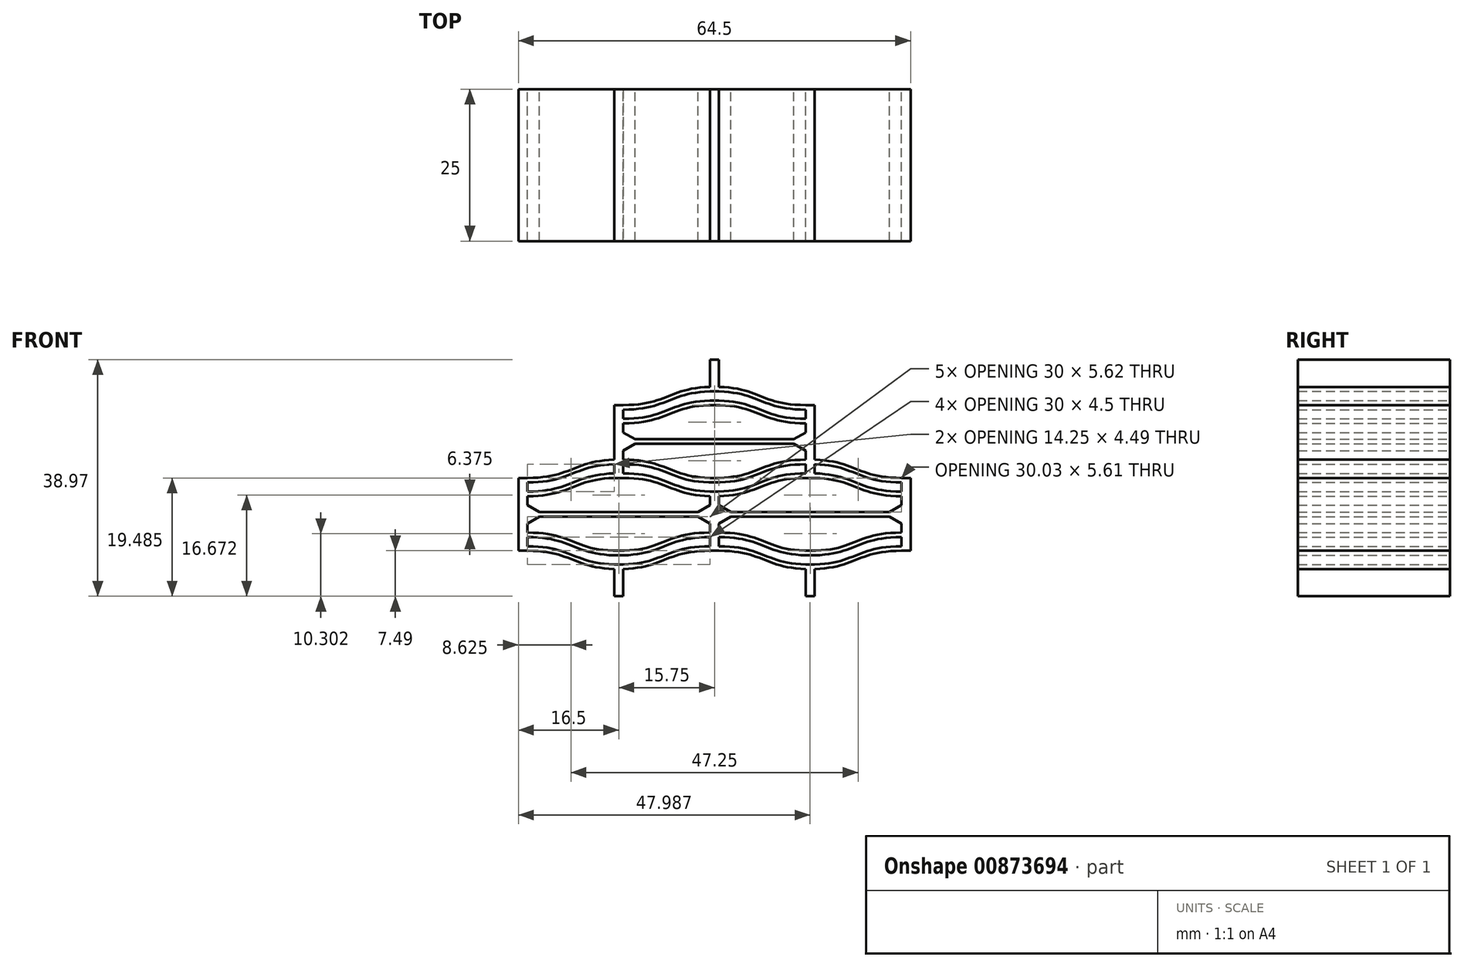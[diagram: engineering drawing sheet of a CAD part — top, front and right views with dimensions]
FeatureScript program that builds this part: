
annotation { "Feature Type Name" : "Feature", "Feature Type Description" : "" }
export const myFeature = defineFeature(function(context is Context, id is Id, definition is map)
    precondition{}
    {
        {
            var Q0;
            Q0=qCreatedBy(makeId("Front.planeOp"),FACE);
            var sketch = newSketch(context, id + "F0", { "sketchPlane" : qUnion([Q0])});
            skLineSegment(sketch, "E0", {"start": v(0, 0) * mm, "end": v(0, -12) * mm});
            skLineSegment(sketch, "E1", {"start": v(0, -12) * mm, "end": v(1.5, -12) * mm});
            skLineSegment(sketch, "E2", {"start": v(0, 0) * mm, "end": v(1.5, 0) * mm});
            skLineSegment(sketch, "E3", {"start": v(33, 0) * mm, "end": v(31.5, 0) * mm});
            skLineSegment(sketch, "E4", {"start": v(33, -12) * mm, "end": v(31.5, -12) * mm});
            skPoint(sketch, "E5", {"position": v(0, -6) * mm});
            skLineSegment(sketch, "E6", {"start": v(1.5, -0.75) * mm, "end": v(1.5, -2.25) * mm});
            skPoint(sketch, "E7", {"position": v(0, -4.5) * mm});
            skPoint(sketch, "E8", {"position": v(0, -7.5) * mm});
            skLineSegment(sketch, "E9", {"start": v(1.5, -7.5) * mm, "end": v(3.45, -6.38) * mm});
            skLineSegment(sketch, "E10", {"start": v(1.5, -4.5) * mm, "end": v(3.45, -5.62) * mm});
            skPoint(sketch, "E11", {"position": v(31.5, -7.5) * mm});
            skPoint(sketch, "E12", {"position": v(31.5, -4.5) * mm});
            skLineSegment(sketch, "E13", {"start": v(31.5, -4.5) * mm, "end": v(29.55, -5.62) * mm});
            skLineSegment(sketch, "E14", {"start": v(29.55, -6.37) * mm, "end": v(31.5, -7.5) * mm});
            skPoint(sketch, "E15.positionSnap0", {"position": v(16.5, -5.62) * mm});
            skPoint(sketch, "E16", {"position": v(0, -3) * mm});
            skPoint(sketch, "E17", {"position": v(0, -9) * mm});
            skPoint(sketch, "E18", {"position": v(0, -2.25) * mm});
            skPoint(sketch, "E19", {"position": v(0, -9.75) * mm});
            skPoint(sketch, "E20", {"position": v(1.5, -0.75) * mm});
            skPoint(sketch, "E21", {"position": v(1.5, -11.25) * mm});
            skPoint(sketch, "E22", {"position": v(1.5, -2.25) * mm});
            skPoint(sketch, "E23", {"position": v(1.5, -3) * mm});
            skPoint(sketch, "E24", {"position": v(1.5, -9.75) * mm});
            skPoint(sketch, "E25", {"position": v(1.5, -9) * mm});
            skPoint(sketch, "E26", {"position": v(31.5, -9) * mm});
            skPoint(sketch, "E27", {"position": v(31.5, -9.75) * mm});
            skPoint(sketch, "E28", {"position": v(31.5, -11.25) * mm});
            skLineSegment(sketch, "E29.trimOffspring", {"start": v(3.45, -5.63) * mm, "end": v(16.5, -5.62) * mm});
            skLineSegment(sketch, "E30.trimOffspring", {"start": v(3.45, -6.38) * mm, "end": v(29.55, -6.37) * mm});
            skPoint(sketch, "E31.start.orphan", {"position": v(0, -6.38) * mm});
            skPoint(sketch, "E32.start.orphan", {"position": v(0, -5.62) * mm});
            skLineSegment(sketch, "E33.trimOffspring", {"start": v(1.5, -3) * mm, "end": v(1.5, -4.5) * mm});
            skLineSegment(sketch, "E34.trimOffspring", {"start": v(1.5, -9.75) * mm, "end": v(1.5, -11.25) * mm});
            skPoint(sketch, "E35.trimOffspring.end.orphan", {"position": v(33, -6.37) * mm});
            skPoint(sketch, "E36.trimOffspring.end.orphan", {"position": v(33, -5.62) * mm});
            skLineSegment(sketch, "E37.trimOffspring", {"start": v(31.5, -9.75) * mm, "end": v(31.5, -11.25) * mm});
            skLineSegment(sketch, "E38.trimOffspring", {"start": v(1.5, -7.5) * mm, "end": v(1.5, -9) * mm});
            skLineSegment(sketch, "E39.trimOffspring", {"start": v(31.5, -7.5) * mm, "end": v(31.5, -9) * mm});
            skLineSegment(sketch, "E40", {"start": v(16.5, -5.62) * mm, "end": v(29.55, -5.62) * mm});
            skPoint(sketch, "E41", {"position": v(16.5, -3) * mm});
            skPoint(sketch, "E42", {"position": v(16.5, 0) * mm});
            skPoint(sketch, "E43", {"position": v(9, -3) * mm});
            skPoint(sketch, "E44", {"position": v(9, -1.5) * mm});
            skPoint(sketch, "E45", {"position": v(24, -1.5) * mm});
            skFitSpline(sketch, "E46", {"points": [v(1.5, -3) * mm, v(9, -1.5) * mm, v(16.5, 0) * mm], "startDerivative": vector(22.5, 0) * mm, "endDerivative": vector(22.5, 0) * mm});
            skFitSpline(sketch, "E47", {"points": [v(16.5, 0) * mm, v(24, -1.5) * mm, v(31.5, -3) * mm], "startDerivative": vector(22.5, 0) * mm, "endDerivative": vector(22.5, 0) * mm});
            skFitSpline(sketch, "E48", {"points": [v(1.5, -2.25) * mm, v(9, -0.75) * mm, v(16.5, 0.75) * mm], "startDerivative": vector(22.5, 0) * mm, "endDerivative": vector(22.5, 0) * mm});
            skFitSpline(sketch, "E49", {"points": [v(1.5, -0.75) * mm, v(9, 0.75) * mm, v(16.5, 2.25) * mm], "startDerivative": vector(22.5, 0) * mm, "endDerivative": vector(22.5, 0) * mm});
            skFitSpline(sketch, "E50", {"points": [v(1.5, 0) * mm, v(9, 1.5) * mm, v(16.5, 3) * mm], "startDerivative": vector(22.5, 0) * mm, "endDerivative": vector(22.5, 0) * mm});
            skFitSpline(sketch, "E51", {"points": [v(31.5, -9) * mm, v(24, -10.5) * mm, v(16.5, -12) * mm], "startDerivative": vector(-22.5, 0) * mm, "endDerivative": vector(-22.5, 0) * mm});
            skFitSpline(sketch, "E52", {"points": [v(16.5, -12) * mm, v(9, -10.5) * mm, v(1.5, -9) * mm], "startDerivative": vector(-22.5, 0) * mm, "endDerivative": vector(-22.5, 0) * mm});
            skFitSpline(sketch, "E53", {"points": [v(31.5, -9.75) * mm, v(24, -11.25) * mm, v(16.5, -12.75) * mm], "startDerivative": vector(-22.5, 0) * mm, "endDerivative": vector(-22.5, 0) * mm});
            skFitSpline(sketch, "E54", {"points": [v(16.5, -12.75) * mm, v(9, -11.25) * mm, v(1.5, -9.75) * mm], "startDerivative": vector(-22.5, 0) * mm, "endDerivative": vector(-22.5, 0) * mm});
            skFitSpline(sketch, "E55", {"points": [v(31.5, -11.25) * mm, v(24, -12.75) * mm, v(16.5, -14.25) * mm], "startDerivative": vector(-22.5, 0) * mm, "endDerivative": vector(-22.5, 0) * mm});
            skFitSpline(sketch, "E56", {"points": [v(16.5, -14.25) * mm, v(9, -12.75) * mm, v(1.5, -11.25) * mm], "startDerivative": vector(-22.5, 0) * mm, "endDerivative": vector(-22.5, 0) * mm});
            skFitSpline(sketch, "E57", {"points": [v(31.5, -12) * mm, v(24, -13.5) * mm, v(16.5, -15) * mm], "startDerivative": vector(-22.5, 0) * mm, "endDerivative": vector(-22.5, 0) * mm});
            skFitSpline(sketch, "E58", {"points": [v(16.5, -15) * mm, v(9, -13.5) * mm, v(1.5, -12) * mm], "startDerivative": vector(-22.5, 0) * mm, "endDerivative": vector(-22.5, 0) * mm});
            skPoint(sketch, "E59", {"position": v(15.75, -12.34) * mm});
            skPoint(sketch, "E60", {"position": v(17.25, -12.34) * mm});
            skLineSegment(sketch, "E61", {"start": v(15.75, -12.74) * mm, "end": v(15.75, -14.24) * mm});
            skLineSegment(sketch, "E62", {"start": v(17.25, -12.74) * mm, "end": v(17.25, -14.24) * mm});
            skLineSegment(sketch, "E63", {"start": v(15.75, -14.99) * mm, "end": v(15.75, -19.49) * mm});
            skLineSegment(sketch, "E64", {"start": v(15.75, 0.74) * mm, "end": v(15.75, 2.24) * mm});
            skLineSegment(sketch, "E65", {"start": v(17.25, 2.24) * mm, "end": v(17.25, 0.74) * mm});
            skLineSegment(sketch, "E66", {"start": v(15.75, -19.49) * mm, "end": v(17.25, -19.49) * mm});
            skLineSegment(sketch, "E67", {"start": v(17.25, -19.49) * mm, "end": v(17.25, -14.99) * mm});
            skPoint(sketch, "E68", {"position": v(15.75, 2.99) * mm});
            skPoint(sketch, "E69", {"position": v(17.25, 2.99) * mm});
            skLineSegment(sketch, "E70", {"start": v(15.75, 2.99) * mm, "end": v(15.75, 7.49) * mm});
            skLineSegment(sketch, "E71", {"start": v(17.25, 4.49) * mm, "end": v(17.25, 2.99) * mm});
            skLineSegment(sketch, "E72", {"start": v(64.5, 0) * mm, "end": v(64.5, -12) * mm});
            skLineSegment(sketch, "E73", {"start": v(31.5, -12) * mm, "end": v(33, -12) * mm});
            skLineSegment(sketch, "E74", {"start": v(31.5, 0) * mm, "end": v(33, 0) * mm});
            skLineSegment(sketch, "E75", {"start": v(64.5, 0) * mm, "end": v(63, 0) * mm});
            skLineSegment(sketch, "E76", {"start": v(64.5, -12) * mm, "end": v(63, -12) * mm});
            skPoint(sketch, "E77", {"position": v(31.5, -6) * mm});
            skLineSegment(sketch, "E78", {"start": v(63, -0.75) * mm, "end": v(63, -2.25) * mm});
            skLineSegment(sketch, "E79", {"start": v(33, -7.5) * mm, "end": v(34.95, -6.37) * mm});
            skLineSegment(sketch, "E80", {"start": v(32.97, -4.5) * mm, "end": v(34.95, -5.62) * mm});
            skPoint(sketch, "E81", {"position": v(63, -7.5) * mm});
            skPoint(sketch, "E82", {"position": v(63, -4.5) * mm});
            skLineSegment(sketch, "E83", {"start": v(63, -4.5) * mm, "end": v(61.05, -5.62) * mm});
            skLineSegment(sketch, "E84", {"start": v(61.05, -6.37) * mm, "end": v(63, -7.5) * mm});
            skPoint(sketch, "E85.positionSnap0", {"position": v(48, -5.62) * mm});
            skPoint(sketch, "E86", {"position": v(33, -11.25) * mm});
            skPoint(sketch, "E87", {"position": v(33, -9.75) * mm});
            skPoint(sketch, "E88", {"position": v(32.97, -9) * mm});
            skPoint(sketch, "E89", {"position": v(63, -0.75) * mm});
            skPoint(sketch, "E90", {"position": v(63, -2.25) * mm});
            skPoint(sketch, "E91", {"position": v(63, -3) * mm});
            skPoint(sketch, "E92", {"position": v(63, -9) * mm});
            skPoint(sketch, "E93", {"position": v(63, -9.75) * mm});
            skPoint(sketch, "E94", {"position": v(63, -11.25) * mm});
            skLineSegment(sketch, "E95.trimOffspring", {"start": v(34.95, -5.62) * mm, "end": v(48, -5.62) * mm});
            skLineSegment(sketch, "E96.trimOffspring", {"start": v(34.95, -6.37) * mm, "end": v(61.05, -6.37) * mm});
            skPoint(sketch, "E97.start.orphan", {"position": v(31.5, -6.37) * mm});
            skPoint(sketch, "E98.start.orphan", {"position": v(31.5, -5.62) * mm});
            skLineSegment(sketch, "E99.trimOffspring", {"start": v(33, -9.75) * mm, "end": v(33, -11.25) * mm});
            skPoint(sketch, "E100.trimOffspring.end.orphan", {"position": v(64.5, -6.37) * mm});
            skPoint(sketch, "E101.trimOffspring.end.orphan", {"position": v(64.5, -5.62) * mm});
            skLineSegment(sketch, "E102.trimOffspring", {"start": v(63, -3) * mm, "end": v(63, -4.5) * mm});
            skLineSegment(sketch, "E103.trimOffspring", {"start": v(63, -9.75) * mm, "end": v(63, -11.25) * mm});
            skLineSegment(sketch, "E104.trimOffspring", {"start": v(33, -7.5) * mm, "end": v(33, -9) * mm});
            skLineSegment(sketch, "E105.trimOffspring", {"start": v(63, -7.5) * mm, "end": v(63, -9) * mm});
            skLineSegment(sketch, "E106", {"start": v(48, -5.62) * mm, "end": v(61.05, -5.62) * mm});
            skPoint(sketch, "E107", {"position": v(48, -3) * mm});
            skPoint(sketch, "E108", {"position": v(48, 0) * mm});
            skPoint(sketch, "E109", {"position": v(40.5, -3) * mm});
            skPoint(sketch, "E110", {"position": v(40.5, -1.5) * mm});
            skPoint(sketch, "E111", {"position": v(55.5, -1.5) * mm});
            skFitSpline(sketch, "E112", {"points": [v(48, 0) * mm, v(55.5, -1.5) * mm, v(63, -3) * mm], "startDerivative": vector(22.5, 0) * mm, "endDerivative": vector(22.5, 0) * mm});
            skFitSpline(sketch, "E113", {"points": [v(48, 0.75) * mm, v(55.5, -0.75) * mm, v(63, -2.25) * mm], "startDerivative": vector(22.5, 0) * mm, "endDerivative": vector(22.5, 0) * mm});
            skFitSpline(sketch, "E114", {"points": [v(48, 2.25) * mm, v(55.5, 0.75) * mm, v(63, -0.75) * mm], "startDerivative": vector(22.5, 0) * mm, "endDerivative": vector(22.5, 0) * mm});
            skFitSpline(sketch, "E115", {"points": [v(48, 3) * mm, v(55.5, 1.5) * mm, v(63, 0) * mm], "startDerivative": vector(22.5, 0) * mm, "endDerivative": vector(22.5, 0) * mm});
            skFitSpline(sketch, "E116", {"points": [v(63, -9) * mm, v(55.5, -10.5) * mm, v(48, -12) * mm], "startDerivative": vector(-22.5, 0) * mm, "endDerivative": vector(-22.5, 0) * mm});
            skFitSpline(sketch, "E117", {"points": [v(48, -12) * mm, v(40.5, -10.5) * mm, v(33, -9) * mm], "startDerivative": vector(-22.5, 0) * mm, "endDerivative": vector(-22.5, 0) * mm});
            skFitSpline(sketch, "E118", {"points": [v(63, -9.75) * mm, v(55.5, -11.25) * mm, v(48, -12.75) * mm], "startDerivative": vector(-22.5, 0) * mm, "endDerivative": vector(-22.5, 0) * mm});
            skFitSpline(sketch, "E119", {"points": [v(48, -12.75) * mm, v(40.5, -11.25) * mm, v(33, -9.75) * mm], "startDerivative": vector(-22.5, 0) * mm, "endDerivative": vector(-22.5, 0) * mm});
            skFitSpline(sketch, "E120", {"points": [v(63, -11.25) * mm, v(55.5, -12.75) * mm, v(48, -14.25) * mm], "startDerivative": vector(-22.5, 0) * mm, "endDerivative": vector(-22.5, 0) * mm});
            skFitSpline(sketch, "E121", {"points": [v(48, -14.25) * mm, v(40.5, -12.75) * mm, v(33, -11.25) * mm], "startDerivative": vector(-22.5, 0) * mm, "endDerivative": vector(-22.5, 0) * mm});
            skFitSpline(sketch, "E122", {"points": [v(63, -12) * mm, v(55.5, -13.5) * mm, v(48, -15) * mm], "startDerivative": vector(-22.5, 0) * mm, "endDerivative": vector(-22.5, 0) * mm});
            skFitSpline(sketch, "E123", {"points": [v(48, -15) * mm, v(40.5, -13.5) * mm, v(33, -12) * mm], "startDerivative": vector(-22.5, 0) * mm, "endDerivative": vector(-22.5, 0) * mm});
            skPoint(sketch, "E124", {"position": v(47.25, -12.34) * mm});
            skPoint(sketch, "E125", {"position": v(48.75, -12.34) * mm});
            skLineSegment(sketch, "E126", {"start": v(47.25, -12.74) * mm, "end": v(47.25, -14.24) * mm});
            skLineSegment(sketch, "E127", {"start": v(48.75, -12.74) * mm, "end": v(48.75, -14.24) * mm});
            skLineSegment(sketch, "E128", {"start": v(47.25, -14.99) * mm, "end": v(47.25, -19.49) * mm});
            skLineSegment(sketch, "E129", {"start": v(47.25, 0.74) * mm, "end": v(47.25, 2.24) * mm});
            skLineSegment(sketch, "E130", {"start": v(48.75, 2.24) * mm, "end": v(48.75, 0.74) * mm});
            skLineSegment(sketch, "E131", {"start": v(47.25, -19.49) * mm, "end": v(48.75, -19.49) * mm});
            skLineSegment(sketch, "E132", {"start": v(48.75, -19.49) * mm, "end": v(48.75, -14.99) * mm});
            skPoint(sketch, "E133", {"position": v(47.25, 2.99) * mm});
            skPoint(sketch, "E134", {"position": v(48.75, 2.99) * mm});
            skLineSegment(sketch, "E135", {"start": v(47.25, 2.99) * mm, "end": v(47.25, 4.49) * mm});
            skLineSegment(sketch, "E136", {"start": v(48.75, 7.49) * mm, "end": v(48.75, 2.99) * mm});
            skLineSegment(sketch, "E137", {"start": v(15.75, 11.99) * mm, "end": v(15.75, 2.99) * mm});
            skLineSegment(sketch, "E138", {"start": v(48.75, 11.99) * mm, "end": v(48.75, 2.99) * mm});
            skLineSegment(sketch, "E139", {"start": v(15.75, -0.01) * mm, "end": v(17.25, -0.01) * mm});
            skLineSegment(sketch, "E140", {"start": v(15.75, 11.99) * mm, "end": v(17.25, 11.99) * mm});
            skLineSegment(sketch, "E141", {"start": v(48.75, 11.99) * mm, "end": v(47.25, 11.99) * mm});
            skLineSegment(sketch, "E142", {"start": v(48.75, -0.01) * mm, "end": v(47.25, -0.01) * mm});
            skPoint(sketch, "E143", {"position": v(15.75, 5.99) * mm});
            skLineSegment(sketch, "E144", {"start": v(17.25, 11.24) * mm, "end": v(17.25, 9.74) * mm});
            skLineSegment(sketch, "E145", {"start": v(47.25, 11.24) * mm, "end": v(47.25, 9.74) * mm});
            skPoint(sketch, "E146", {"position": v(15.75, 7.49) * mm});
            skPoint(sketch, "E147", {"position": v(15.75, 4.49) * mm});
            skLineSegment(sketch, "E148", {"start": v(17.25, 4.49) * mm, "end": v(19.2, 5.61) * mm});
            skLineSegment(sketch, "E149", {"start": v(17.25, 7.49) * mm, "end": v(19.2, 6.36) * mm});
            skPoint(sketch, "E150", {"position": v(47.25, 4.49) * mm});
            skPoint(sketch, "E151", {"position": v(47.25, 7.49) * mm});
            skLineSegment(sketch, "E152", {"start": v(47.25, 7.49) * mm, "end": v(45.3, 6.36) * mm});
            skLineSegment(sketch, "E153", {"start": v(45.3, 5.61) * mm, "end": v(47.25, 4.49) * mm});
            skPoint(sketch, "E154.positionSnap0", {"position": v(32.25, 6.36) * mm});
            skPoint(sketch, "E155", {"position": v(15.75, 8.99) * mm});
            skPoint(sketch, "E156", {"position": v(15.75, 9.74) * mm});
            skPoint(sketch, "E157", {"position": v(15.75, 2.24) * mm});
            skPoint(sketch, "E158", {"position": v(17.25, 11.24) * mm});
            skPoint(sketch, "E159", {"position": v(17.25, 0.74) * mm});
            skPoint(sketch, "E160", {"position": v(17.25, 9.74) * mm});
            skPoint(sketch, "E161", {"position": v(17.25, 8.99) * mm});
            skPoint(sketch, "E162", {"position": v(17.25, 2.24) * mm});
            skPoint(sketch, "E163", {"position": v(47.25, 11.24) * mm});
            skPoint(sketch, "E164", {"position": v(47.25, 9.74) * mm});
            skPoint(sketch, "E165", {"position": v(47.25, 8.99) * mm});
            skPoint(sketch, "E166", {"position": v(47.25, 2.24) * mm});
            skPoint(sketch, "E167", {"position": v(47.25, 0.74) * mm});
            skLineSegment(sketch, "E168.trimOffspring", {"start": v(19.2, 6.36) * mm, "end": v(32.25, 6.36) * mm});
            skLineSegment(sketch, "E169.trimOffspring", {"start": v(19.2, 5.61) * mm, "end": v(45.3, 5.61) * mm});
            skPoint(sketch, "E170.start.orphan", {"position": v(15.75, 5.61) * mm});
            skPoint(sketch, "E171.start.orphan", {"position": v(15.75, 6.36) * mm});
            skLineSegment(sketch, "E172.trimOffspring", {"start": v(17.25, 8.99) * mm, "end": v(17.25, 7.49) * mm});
            skPoint(sketch, "E173.trimOffspring.end.orphan", {"position": v(48.75, 5.61) * mm});
            skPoint(sketch, "E174.trimOffspring.end.orphan", {"position": v(48.75, 6.36) * mm});
            skLineSegment(sketch, "E175.trimOffspring", {"start": v(47.25, 8.99) * mm, "end": v(47.25, 7.49) * mm});
            skLineSegment(sketch, "E176.trimOffspring", {"start": v(47.25, 2.24) * mm, "end": v(47.25, 0.74) * mm});
            skLineSegment(sketch, "E177.trimOffspring", {"start": v(47.25, 4.49) * mm, "end": v(47.25, 2.99) * mm});
            skLineSegment(sketch, "E178", {"start": v(32.25, 6.36) * mm, "end": v(45.3, 6.36) * mm});
            skPoint(sketch, "E179", {"position": v(32.25, 8.99) * mm});
            skPoint(sketch, "E180", {"position": v(32.25, 11.99) * mm});
            skPoint(sketch, "E181", {"position": v(24.75, 8.99) * mm});
            skPoint(sketch, "E182", {"position": v(24.75, 10.49) * mm});
            skPoint(sketch, "E183", {"position": v(39.75, 10.49) * mm});
            skFitSpline(sketch, "E184", {"points": [v(17.25, 8.99) * mm, v(24.75, 10.49) * mm, v(32.25, 11.99) * mm], "startDerivative": vector(22.5, 0) * mm, "endDerivative": vector(22.5, 0) * mm});
            skFitSpline(sketch, "E185", {"points": [v(32.25, 11.99) * mm, v(39.75, 10.49) * mm, v(47.25, 8.99) * mm], "startDerivative": vector(22.5, 0) * mm, "endDerivative": vector(22.5, 0) * mm});
            skFitSpline(sketch, "E186", {"points": [v(17.25, 9.74) * mm, v(24.75, 11.24) * mm, v(32.25, 12.74) * mm], "startDerivative": vector(22.5, 0) * mm, "endDerivative": vector(22.5, 0) * mm});
            skFitSpline(sketch, "E187", {"points": [v(32.25, 12.74) * mm, v(39.75, 11.24) * mm, v(47.25, 9.74) * mm], "startDerivative": vector(22.5, 0) * mm, "endDerivative": vector(22.5, 0) * mm});
            skFitSpline(sketch, "E188", {"points": [v(17.25, 11.24) * mm, v(24.75, 12.74) * mm, v(32.25, 14.24) * mm], "startDerivative": vector(22.5, 0) * mm, "endDerivative": vector(22.5, 0) * mm});
            skFitSpline(sketch, "E189", {"points": [v(32.25, 14.24) * mm, v(39.75, 12.74) * mm, v(47.25, 11.24) * mm], "startDerivative": vector(22.5, 0) * mm, "endDerivative": vector(22.5, 0) * mm});
            skFitSpline(sketch, "E190", {"points": [v(17.25, 11.99) * mm, v(24.75, 13.49) * mm, v(32.25, 14.99) * mm], "startDerivative": vector(22.5, 0) * mm, "endDerivative": vector(22.5, 0) * mm});
            skFitSpline(sketch, "E191", {"points": [v(32.25, 14.99) * mm, v(39.75, 13.49) * mm, v(47.25, 11.99) * mm], "startDerivative": vector(22.5, 0) * mm, "endDerivative": vector(22.5, 0) * mm});
            skFitSpline(sketch, "E192", {"points": [v(47.25, 2.99) * mm, v(39.75, 1.49) * mm, v(32.25, -0.01) * mm], "startDerivative": vector(-22.5, 0) * mm, "endDerivative": vector(-22.5, 0) * mm});
            skFitSpline(sketch, "E193", {"points": [v(32.25, -0.01) * mm, v(24.75, 1.49) * mm, v(17.25, 2.99) * mm], "startDerivative": vector(-22.5, 0) * mm, "endDerivative": vector(-22.5, 0) * mm});
            skFitSpline(sketch, "E194", {"points": [v(47.25, 2.24) * mm, v(39.75, 0.74) * mm, v(32.25, -0.76) * mm], "startDerivative": vector(-22.5, 0) * mm, "endDerivative": vector(-22.5, 0) * mm});
            skFitSpline(sketch, "E195", {"points": [v(32.25, -0.76) * mm, v(24.75, 0.74) * mm, v(17.25, 2.24) * mm], "startDerivative": vector(-22.5, 0) * mm, "endDerivative": vector(-22.5, 0) * mm});
            skFitSpline(sketch, "E196", {"points": [v(47.25, 0.74) * mm, v(39.75, -0.76) * mm, v(32.25, -2.26) * mm], "startDerivative": vector(-22.5, 0) * mm, "endDerivative": vector(-22.5, 0) * mm});
            skFitSpline(sketch, "E197", {"points": [v(32.25, -2.26) * mm, v(24.75, -0.76) * mm, v(17.25, 0.74) * mm], "startDerivative": vector(-22.5, 0) * mm, "endDerivative": vector(-22.5, 0) * mm});
            skFitSpline(sketch, "E198", {"points": [v(47.25, -0.01) * mm, v(39.75, -1.51) * mm, v(32.25, -3.01) * mm], "startDerivative": vector(-22.5, 0) * mm, "endDerivative": vector(-22.5, 0) * mm});
            skFitSpline(sketch, "E199", {"points": [v(32.25, -3.01) * mm, v(24.75, -1.51) * mm, v(17.25, -0.01) * mm], "startDerivative": vector(-22.5, 0) * mm, "endDerivative": vector(-22.5, 0) * mm});
            skLineSegment(sketch, "E200", {"start": v(31.5, 12.73) * mm, "end": v(31.5, 14.23) * mm});
            skLineSegment(sketch, "E201", {"start": v(33, 14.23) * mm, "end": v(33, 12.73) * mm});
            skPoint(sketch, "E202", {"position": v(31.5, 14.98) * mm});
            skPoint(sketch, "E203", {"position": v(33, 14.98) * mm});
            skLineSegment(sketch, "E204", {"start": v(31.5, 14.98) * mm, "end": v(31.5, 19.48) * mm});
            skLineSegment(sketch, "E205", {"start": v(31.5, 19.48) * mm, "end": v(33, 19.48) * mm});
            skLineSegment(sketch, "E206", {"start": v(33, 19.48) * mm, "end": v(33, 14.98) * mm});
            skPoint(sketch, "E207.startDerivative.orphan", {"position": v(20.25, 3) * mm});
            skPoint(sketch, "E208.startDerivative.orphan", {"position": v(20.25, 2.25) * mm});
            skPoint(sketch, "E209.startDerivative.orphan", {"position": v(20.25, 0.75) * mm});
            skPoint(sketch, "E210.end.orphan", {"position": v(17.25, 7.49) * mm});
            skPoint(sketch, "E211.orphan", {"position": v(33, -7.5) * mm});
            skLineSegment(sketch, "E212", {"start": v(31.5, -4.5) * mm, "end": v(31.5, -3) * mm});
            skLineSegment(sketch, "E213", {"start": v(32.97, -4.5) * mm, "end": v(32.97, -3) * mm});
            skLineSegment(sketch, "E214", {"start": v(31.5, -2.25) * mm, "end": v(31.5, -1.4) * mm});
            skLineSegment(sketch, "E215", {"start": v(32.97, -2.25) * mm, "end": v(32.97, -1.4) * mm});
            skSolve(sketch);
        }
        {
            var Q0;
            Q0 = qSketchRegion(id + "F0", true);
            extrude(context, id + "F1", {"entities" : qUnion([Q0]), "depth" : 25 * mm, "offsetDistance" : 25 * mm});
        }
    });
